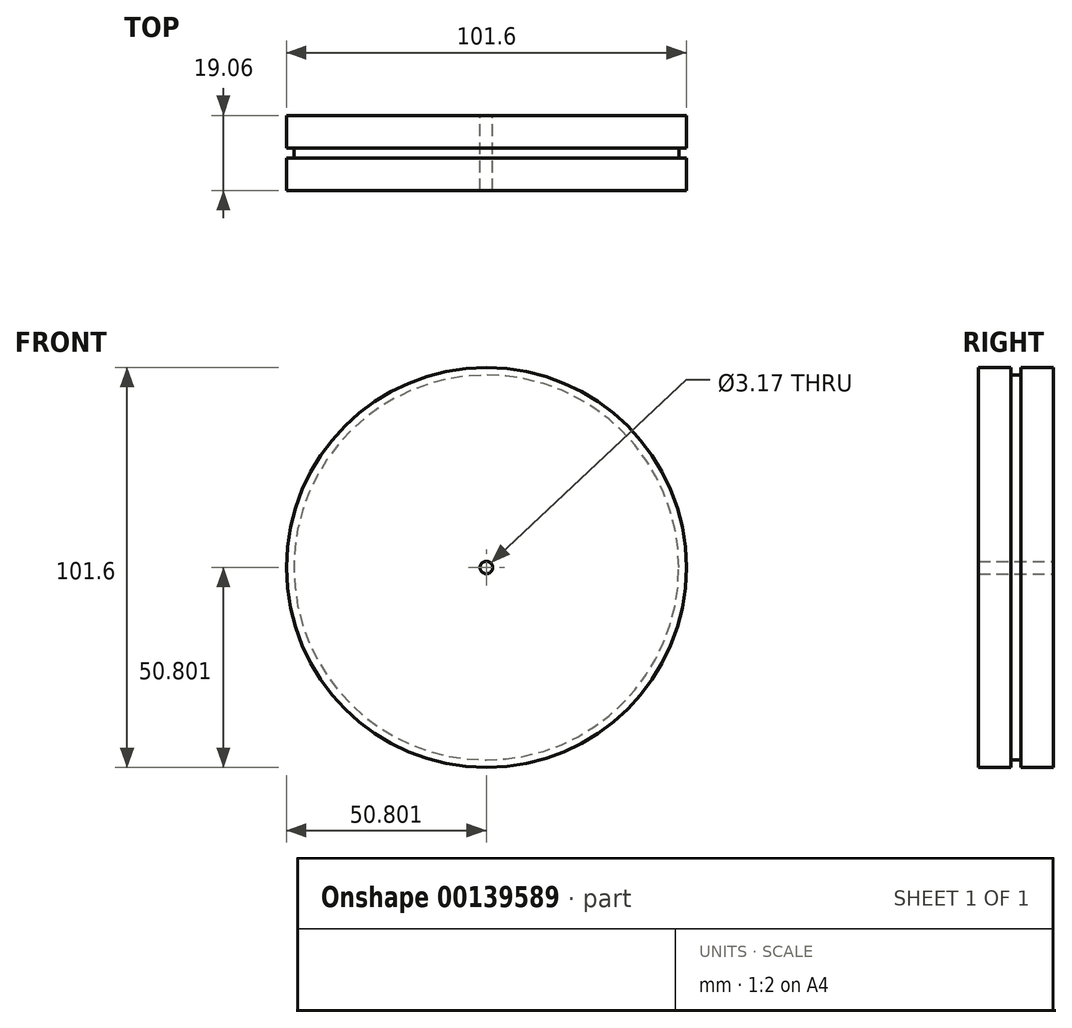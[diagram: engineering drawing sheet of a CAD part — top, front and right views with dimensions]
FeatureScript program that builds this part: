
annotation { "Feature Type Name" : "Feature", "Feature Type Description" : "" }
export const myFeature = defineFeature(function(context is Context, id is Id, definition is map)
    precondition{}
    {
        {
            var Q0;
            Q0=qCreatedBy(makeId("Front.planeOp"),FACE);
            var sketch = newSketch(context, id + "F0", { "sketchPlane" : qUnion([Q0])});
            skCircle(sketch, "E0", {"center": v(-23.89, 6.38) * mm, "radius": 50.8 * mm});
            skCircle(sketch, "E1", {"center": v(-23.89, 6.38) * mm, "radius": 1.59 * mm});
            skCircle(sketch, "E2", {"center": v(-23.89, 6.38) * mm, "radius": 48.9 * mm});
            skSolve(sketch);
        }
        {
            var Q0;
            Q0=makeQuery(id+"F0.imprint","IMPRINT",FACE,{"disambiguationData":[TD([[makeQuery(id+"F0.imprint","IMPRINT",EDGE,{"derivedFrom":sQuery(id+"F0.wireOp",EDGE,"E1")}),-1.0]])]});
            extrude(context, id + "F1", {"entities" : qUnion([Q0]), "endBound" : BoundingType.SYMMETRIC, "depth" : 19.05 * mm});
        }
        {
            var Q0;
            Q0=makeQuery(id+"F0.imprint","IMPRINT",FACE,{"disambiguationData":[TD([[makeQuery(id+"F0.imprint","IMPRINT",EDGE,{"derivedFrom":sQuery(id+"F0.wireOp",EDGE,"E0")}),1.0]])]});
            extrude(context, id + "F2", {"entities" : qUnion([Q0]), "operationType" : NewBodyOperationType.ADD, "endBound" : BoundingType.SYMMETRIC, "oppositeDirection" : true, "depth" : 19.05 * mm});
        }
        {
            var Q0;
            Q0=makeQuery(id+"F0.imprint","IMPRINT",FACE,{"disambiguationData":[TD([[makeQuery(id+"F0.imprint","IMPRINT",EDGE,{"derivedFrom":sQuery(id+"F0.wireOp",EDGE,"E0")}),1.0]])]});
            extrude(context, id + "F3", {"entities" : qUnion([Q0]), "operationType" : NewBodyOperationType.REMOVE, "endBound" : BoundingType.SYMMETRIC, "oppositeDirection" : true, "depth" : 2.54 * mm});
        }
    });
